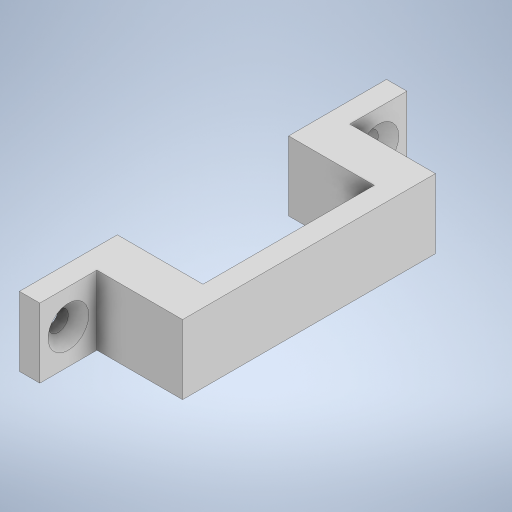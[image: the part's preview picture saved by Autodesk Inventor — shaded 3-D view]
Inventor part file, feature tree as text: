
AUTODESK INVENTOR PART (.ipt)
format: ipt  version: 2024 (Build 280153000, 153)  size: 296,960 bytes
history: native  units: mm
features: sketch x7, extrude x6, other x3, move_body x2, surface_op x1, hole x1, imported_body x1
ambient origin geometry x8: Origin, YZ Plane, XZ Plane, XY Plane, X Axis, Y Axis, Z Axis, Center Point
bodies: Solid1 (feature_tree), Solid2 (feature_tree)
feature tree (21):
  other  "Repaired Geometry1"
  extrude  "Extrusion1"  Depth=42.0mm
  move_body  "Move Body1"
  extrude  "Extrusion2"  Depth=10.0mm TaperAngle=0.0deg
  extrude  "Extrusion3"  Depth=26.0mm
  extrude  "Extrusion4"  Depth=26.0mm
  move_body  "Move Body2"
  surface_op  "Sculpt1"
  extrude  "Extrusion5"  TaperAngle=0.0deg  [1 undecoded]
  extrude  "Extrusion6"  Depth=14.0mm TaperAngle=0.0deg
  hole  "Hole3"  [1 undecoded]
  sketch  "Sketch1"  dims[d0=17.0mm d1=42.0mm]
  imported_body  "Base1"
  sketch  "Sketch2"  dims[d2=21.0mm d3=0.0mm d4=10.0mm d5=0.0mm d6=0.0mm]
  sketch  "Sketch3"  dims[d7=5.0mm d8=0.0mm d9=26.0mm]
  sketch  "Sketch4"  dims[d10=10.0mm d11=0.0mm d12=26.0mm]
  sketch  "Sketch5"  dims[d13=10.0mm d14=0.0mm d15=-10.0mm d16=0.0mm d17=0.0mm]
  sketch  "Sketch6"  dims[d18=5.0mm d19=14.0mm d20=0.0mm]
  sketch  "Sketch9"  dims[d21=5.0mm d22=14.0mm d23=0.0mm d40=7.0mm d41=7.0mm d42=5.0mm d43=6.0mm d44=10.0mm d45=2.0mm d46=90.0deg d47=8.0mm d48=20.594885mm]
  other  "Composite1"
  other  "Srf1"
note: 2 required parameter values undecoded (feature->parameter linkage not recoverable at this tier; creation-order binding heuristic only, values carry confidence <= 0.55)
